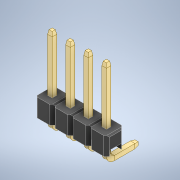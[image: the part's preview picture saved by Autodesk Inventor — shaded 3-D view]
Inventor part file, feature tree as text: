
AUTODESK INVENTOR PART (.ipt)
format: ipt  version: 2021 (Build 250183000, 183)  size: 235,520 bytes
history: native  units: in
note: dims shown in document units (in); Inventor stores cm internally (conversion verified against a paired STEP export)
features: other x3, chamfer x1, boolean_combine x1
ambient origin geometry x8: Origin, YZ Plane, XZ Plane, XY Plane, X Axis, Y Axis, Z Axis, Center Point
bodies: Solid1 (feature_tree), Solid2 (feature_tree), Solid3 (feature_tree), Solid4 (feature_tree), Solid5 (feature_tree)
feature tree (5):
  chamfer  "Chamfer3"  [1 undecoded]
  other  "LPattern1[1]"
  other  "LPattern1[2]"
  other  "LPattern1[3]"
  boolean_combine  "Combine1"
note: 1 required parameter value undecoded (feature->parameter linkage not recoverable at this tier; creation-order binding heuristic only, values carry confidence <= 0.55)
